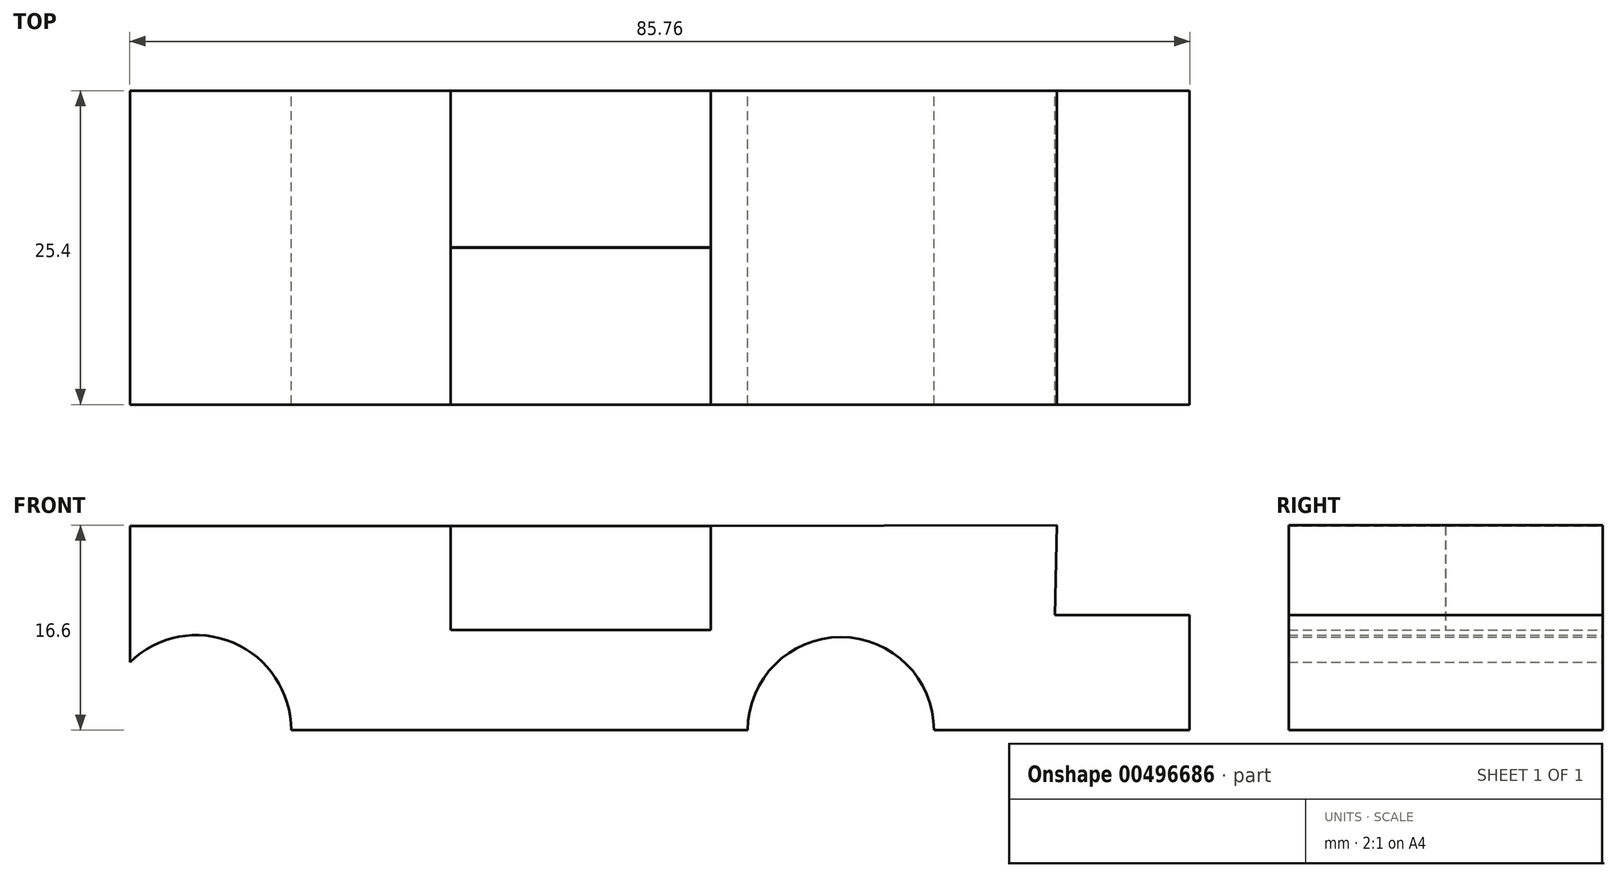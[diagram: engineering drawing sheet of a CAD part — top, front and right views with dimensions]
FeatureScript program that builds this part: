
annotation { "Feature Type Name" : "Feature", "Feature Type Description" : "" }
export const myFeature = defineFeature(function(context is Context, id is Id, definition is map)
    precondition{}
    {
        {
            var Q0;
            Q0=qCreatedBy(makeId("Front.planeOp"),FACE);
            var sketch = newSketch(context, id + "F0", { "sketchPlane" : qUnion([Q0])});
            skLineSegment(sketch, "E0.bottom", {"start": v(-22.62, -6.42) * mm, "end": v(31.35, -6.42) * mm});
            skLineSegment(sketch, "E0.top", {"start": v(-22.62, -14.52) * mm, "end": v(31.35, -14.52) * mm});
            skLineSegment(sketch, "E1.bottom", {"start": v(-22.62, -14.52) * mm, "end": v(-30.89, -14.52) * mm});
            skLineSegment(sketch, "E1.top", {"start": v(-22.62, 2) * mm, "end": v(-31.1, 2) * mm});
            skLineSegment(sketch, "E2.bottom", {"start": v(-22.62, 2) * mm, "end": v(-4.92, 2) * mm});
            skLineSegment(sketch, "E2.top", {"start": v(-22.62, -6.42) * mm, "end": v(-4.92, -6.42) * mm});
            skLineSegment(sketch, "E2.right", {"start": v(-4.92, 2) * mm, "end": v(-4.92, -6.42) * mm});
            skLineSegment(sketch, "E3.right", {"start": v(16.1, -6.42) * mm, "end": v(16.1, 2) * mm});
            skCircle(sketch, "E4", {"center": v(-25.53, -14.52) * mm, "radius": 7.7 * mm});
            skCircle(sketch, "E5", {"center": v(26.64, -14.52) * mm, "radius": 7.54 * mm});
            skLineSegment(sketch, "E6", {"start": v(-4.92, 2) * mm, "end": v(16.1, 2) * mm});
            skLineSegment(sketch, "E7", {"start": v(-30.89, -14.52) * mm, "end": v(-30.89, 2) * mm});
            skLineSegment(sketch, "E8", {"start": v(31.35, -14.52) * mm, "end": v(48.13, -14.52) * mm});
            skLineSegment(sketch, "E9", {"start": v(48.13, -14.52) * mm, "end": v(54.87, -14.52) * mm});
            skLineSegment(sketch, "E10", {"start": v(54.87, -14.52) * mm, "end": v(54.87, -5.19) * mm});
            skLineSegment(sketch, "E11", {"start": v(54.87, -5.19) * mm, "end": v(43.95, -5.19) * mm});
            skLineSegment(sketch, "E12", {"start": v(43.95, -5.19) * mm, "end": v(44.1, 2.08) * mm});
            skLineSegment(sketch, "E13", {"start": v(16.1, 2) * mm, "end": v(44.1, 2.08) * mm});
            skSolve(sketch);
        }
        {
            var Q0;
            Q0=makeQuery(id+"F0.imprint","IMPRINT",FACE,{"disambiguationData":[TD([[makeQuery(id+"F0.imprint","IMPRINT",EDGE,{"derivedFrom":sQuery(id+"F0.wireOp",EDGE,"E0.bottom")}),1.0]])]});
            extrude(context, id + "F1", {"entities" : qUnion([Q0]), "endBound" : BoundingType.SYMMETRIC, "depth" : 1 / 101.6 * mm});
        }
        {
            var Q0;
            Q0=makeQuery(id+"F0.imprint","IMPRINT",FACE,{"disambiguationData":[TD([[makeQuery(id+"F0.imprint","IMPRINT",EDGE,{"derivedFrom":sQuery(id+"F0.wireOp",EDGE,"E2.bottom")}),-1.0]])]});
            extrude(context, id + "F2", {"entities" : qUnion([Q0]), "operationType" : NewBodyOperationType.ADD, "endBound" : BoundingType.SYMMETRIC, "depth" : 25.4 * mm});
        }
        {
            var Q0;
            {var subQ1=sQuery(id+"F0.wireOp",EDGE,"E1.top");Q0=makeQuery(id+"F0.imprint","IMPRINT",FACE,{"disambiguationData":[TD([[makeQuery(id+"F0.imprint","IMPRINT",EDGE,{"derivedFrom":subQ1}),1.0]])]});}
            extrude(context, id + "F3", {"entities" : qUnion([Q0]), "operationType" : NewBodyOperationType.ADD, "endBound" : BoundingType.SYMMETRIC, "depth" : 25.4 * mm});
        }
        {
            var Q0;
            Q0=makeQuery(id+"F0.imprint","IMPRINT",FACE,{"disambiguationData":[TD([[makeQuery(id+"F0.imprint","IMPRINT",EDGE,{"derivedFrom":sQuery(id+"F0.wireOp",EDGE,"E0.bottom")}),-1.0]])]});
            extrude(context, id + "F4", {"entities" : qUnion([Q0]), "operationType" : NewBodyOperationType.ADD, "endBound" : BoundingType.SYMMETRIC, "depth" : 25.4 * mm});
        }
        {
            var Q0;
            {var subQ0=sQuery(id+"F0.wireOp",EDGE,"E2.right");Q0=makeQuery(id+"F0.imprint","IMPRINT",FACE,{"disambiguationData":[TD([[makeQuery(id+"F0.imprint","IMPRINT",EDGE,{"derivedFrom":subQ0}),1.0]])]});}
            extrude(context, id + "F5", {"entities" : qUnion([Q0]), "endBound" : BoundingType.SYMMETRIC, "depth" : 1 / 101.6 * mm});
        }
        {
            var Q0;
            Q0=sQuery(id+"F0.wireOp",EDGE,"E4");
            extrude(context, id + "F6", {"bodyType" : ToolBodyType.SURFACE, "surfaceEntities" : qUnion([Q0]), "oppositeDirection" : true, "depth" : 12.7 * mm, "hasSecondDirection" : true, "secondDirectionOppositeDirection" : false, "secondDirectionDepth" : 12.45 * mm});
        }
        {
            var Q0;
            Q0=sQuery(id+"F0.wireOp",EDGE,"E5");
            extrude(context, id + "F7", {"bodyType" : ToolBodyType.SURFACE, "surfaceEntities" : qUnion([Q0]), "endBound" : BoundingType.SYMMETRIC, "depth" : 25.4 * mm});
        }
    });
